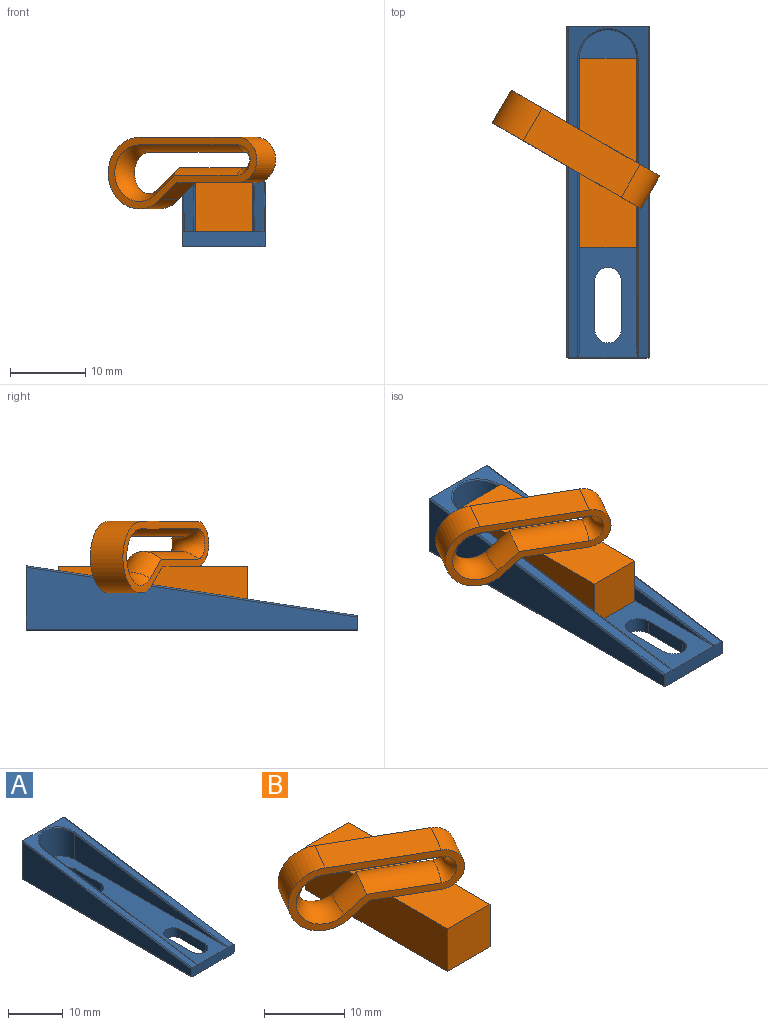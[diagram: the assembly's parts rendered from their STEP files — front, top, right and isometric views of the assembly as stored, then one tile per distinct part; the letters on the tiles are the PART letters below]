
ASSEMBLY  parts=2 mates=1
PART A: 25 faces, bbox 11x44.1x8.6 mm
  f0: plane 44x10.6mm, normal (0,0,-1), area 401.7mm2, adj f2,f3,f13,f15,f17,f18,f19,f20
  f1: plane 43.5x8mm, normal (0,0,1), area 259.8mm2, adj f2,f7,f8,f9,f10,f12,f17,f18
  f2: plane 11.01x2.01mm, normal (0,-1,0), area 22mm2, adj f0,f1,f4,f5,f6,f13,f14,f15
  f3: plane 11.01x8.61mm, normal (0,1,0), area 94.6mm2, adj f0,f4,f5,f6,f13,f14,f15,f16
  f4: plane 44x10.6mm, normal (0,-0.15,0.99), area 125.3mm2, adj f2,f3,f10,f11,f12,f14,f16
  f5: plane 44x8.2mm, normal (1,0,0), area 215.5mm2, adj f2,f3,f15,f16
  f6: plane 44x8.2mm, normal (-1,0,0), area 215.5mm2, adj f2,f3,f13,f14
  f7: plane 38.35x5.75mm, normal (-1,0,0), area 110.3mm2, adj f1,f8,f12
  f8: cylinder r=3.8mm len=7.6mm, axis (0,0,-1), area 73.2mm2, adj f1,f7,f9,f11
  f9: plane 38.35x5.75mm, normal (1,0,0), area 110.3mm2, adj f1,f8,f10
  f10: cylinder r=0.2mm len=39.7mm, axis (0,0.99,0.15), area 12.4mm2, adj f1,f4,f9,f11
  f11: bspline ~8x4.7mm, area 3.6mm2, adj f4,f8,f10,f12
  f12: cylinder r=0.2mm len=39.7mm, axis (0,-0.99,-0.15), area 12.5mm2, adj f1,f4,f7,f11
  f13: cylinder r=0.2mm len=44mm, axis (0,1,0), area 13.8mm2, adj f0,f2,f3,f6
  f14: cylinder r=0.2mm len=44.06mm, axis (0,-0.99,-0.15), area 14mm2, adj f2,f3,f4,f6
  f15: cylinder r=0.2mm len=44mm, axis (0,-1,0), area 13.8mm2, adj f0,f2,f3,f5
  f16: cylinder r=0.2mm len=44.06mm, axis (0,0.99,0.15), area 14mm2, adj f2,f3,f4,f5
  f17: plane 6.5x2mm, normal (1,0,0), area 13mm2, adj f0,f1,f18,f20
  f18: cylinder r=1.75mm len=3.5mm, axis (0,0,1), area 11mm2, adj f0,f1,f17,f19
  f19: plane 6.5x2mm, normal (-1,0,0), area 13mm2, adj f0,f1,f18,f20
  f20: cylinder r=1.75mm len=3.5mm, axis (0,0,1), area 11mm2, adj f0,f1,f17,f19
  f21: plane 6.5x2mm, normal (1,0,0), area 13mm2, adj f0,f1,f22,f24
  f22: cylinder r=1.75mm len=3.5mm, axis (0,0,1), area 11mm2, adj f0,f1,f21,f23
  f23: plane 6.5x2mm, normal (-1,0,0), area 13mm2, adj f0,f1,f22,f24
  f24: cylinder r=1.75mm len=3.5mm, axis (0,0,1), area 11mm2, adj f0,f1,f21,f23
PART B: 20 faces, bbox 22.2x25x12.5 mm
  f0: plane 1.16x0.5mm, normal (0,0,-1), area 0.3mm2, adj f4,f5,f14
  f1: plane 5.77x2.5mm, normal (0,0,-1), area 7.2mm2, adj f2,f9,f16
  f2: plane 19.7x11.38mm, normal (-0.5,-0.87,0), area 52.4mm2, adj f1,f3,f5,f6,f7,f8,f9,f10
  f3: cylinder r=3.62mm len=11.16mm, axis (0.87,-0.5,0), area 54.5mm2, adj f2,f4,f6,f10
  f4: plane 19.7x11.38mm, normal (0.5,0.87,0), area 52.4mm2, adj f0,f3,f5,f6,f7,f8,f9,f10
  f5: cylinder r=3mm len=6mm, axis (-0.5,-0.87,0), area 47.1mm2, adj f0,f2,f4,f8,f13
  f6: torus R=4.62mm, axis (-0.5,-0.87,0), area 23.2mm2, adj f2,f3,f4,f7
  f7: cylinder r=3.62mm len=15.49mm, axis (-0.87,0.5,0), area 82.8mm2, adj f2,f4,f6,f12
  f8: plane 15.49x11.83mm, normal (0,0,1), area 75mm2, adj f2,f4,f5,f11
  f9: plane 5.64x4.76mm, normal (0.57,-0.33,-0.75), area 17.4mm2, adj f1,f2,f4,f11
  f10: cylinder r=3.62mm len=5.92mm, axis (0.65,-0.37,0.66), area 22.7mm2, adj f2,f3,f4,f12
  f11: cylinder r=4.75mm len=9.5mm, axis (-0.5,-0.87,0), area 91.8mm2, adj f2,f4,f8,f9
  f12: torus R=6.38mm, axis (-0.5,-0.87,0), area 65.9mm2, adj f2,f4,f7,f10
  f13: plane 10.04x7.5mm, normal (0,0,1), area 61.6mm2, adj f2,f5,f14,f16,f18
  f14: plane 25x6.5mm, normal (1,0,0), area 162.5mm2, adj f0,f13,f15,f17,f18,f19
  f15: plane 13.79x7.5mm, normal (0,0,1), area 87.2mm2, adj f4,f14,f16,f19
  f16: plane 25x6.5mm, normal (-1,0,0), area 162.5mm2, adj f1,f13,f15,f17,f18,f19
  f17: plane 25x7.5mm, normal (0,0,-1), area 187.5mm2, adj f14,f16,f18,f19
  f18: plane 7.5x6.5mm, normal (0,-1,0), area 48.8mm2, adj f13,f14,f16,f17
  f19: plane 7.5x6.5mm, normal (0,1,0), area 48.8mm2, adj f14,f15,f16,f17
PLACE A t=(-12.03,11.41,-11.82)mm fixed
PLACE B t=(-15.52,-5.39,0.68)mm
MATE fastened B.f17 <-> A.f8  axis (0,0,-1) through (-12.03,7.11,-9.82)mm
